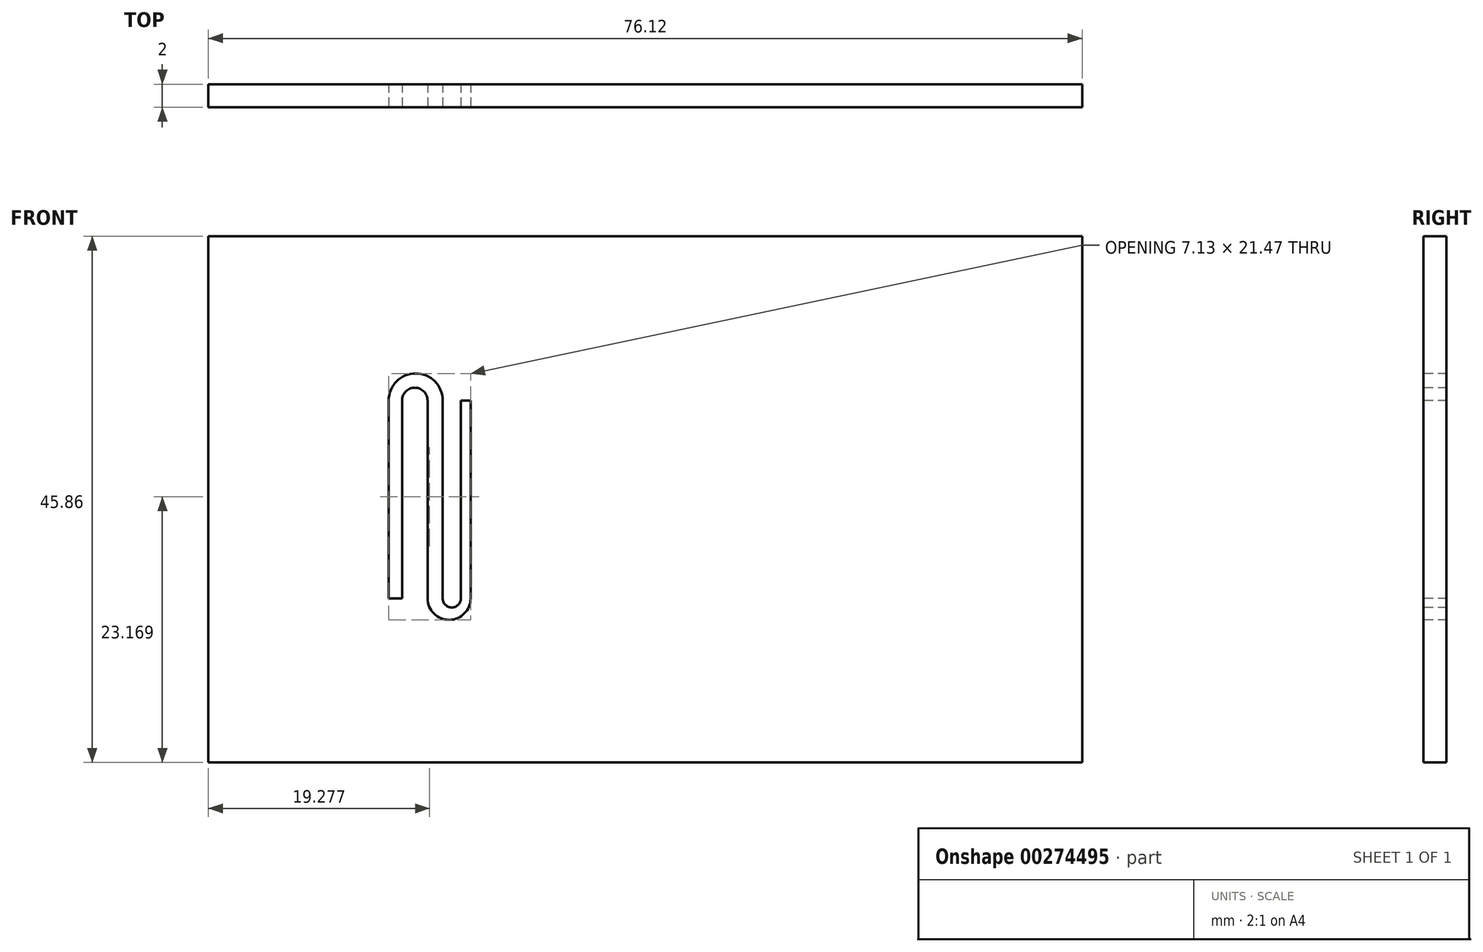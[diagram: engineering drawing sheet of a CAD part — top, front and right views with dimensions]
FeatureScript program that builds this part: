
annotation { "Feature Type Name" : "Feature", "Feature Type Description" : "" }
export const myFeature = defineFeature(function(context is Context, id is Id, definition is map)
    precondition{}
    {
        {
            var Q0;
            Q0=qCreatedBy(makeId("Front.planeOp"),FACE);
            var sketch = newSketch(context, id + "F0", { "sketchPlane" : qUnion([Q0])});
            skLineSegment(sketch, "E0.bottom", {"start": v(38.06, -22.93) * mm, "end": v(-38.06, -22.93) * mm});
            skLineSegment(sketch, "E0.top", {"start": v(38.06, 22.93) * mm, "end": v(-38.06, 22.93) * mm});
            skLineSegment(sketch, "E0.left", {"start": v(38.06, -22.93) * mm, "end": v(38.06, 22.93) * mm});
            skLineSegment(sketch, "E0.right", {"start": v(-38.06, -22.93) * mm, "end": v(-38.06, 22.93) * mm});
            skPoint(sketch, "E0.middle", {"position": v(0, 0) * mm});
            skSolve(sketch);
        }
        {
            var Q0;
            Q0=makeQuery(id+"F0.imprint","IMPRINT",FACE,{"disambiguationData":[TD([[makeQuery(id+"F0.imprint","IMPRINT",EDGE,{"derivedFrom":sQuery(id+"F0.wireOp",EDGE,"E0.bottom")}),-1.0]])]});
            extrude(context, id + "F1", {"entities" : qUnion([Q0]), "depth" : 2 * mm});
        }
        {
            var Q0;
            Q0=makeQuery(id+"F1.opExtrude","CAP_FACE",FACE,{"disambiguationData":[OSD([sQuery(id+"F0.wireOp",EDGE,"E0.bottom"),sQuery(id+"F0.wireOp",EDGE,"E0.top"),sQuery(id+"F0.wireOp",EDGE,"E0.left"),sQuery(id+"F0.wireOp",EDGE,"E0.right")])],"isStart":false});
            var sketch = newSketch(context, id + "F2", { "sketchPlane" : qUnion([Q0])});
            skLineSegment(sketch, "E1.left", {"start": v(21.19, -8.62) * mm, "end": v(21.19, 8.62) * mm});
            skLineSegment(sketch, "E1.right", {"start": v(-21.19, -8.62) * mm, "end": v(-21.19, 8.62) * mm});
            skPoint(sketch, "E1.middle", {"position": v(0, 0) * mm});
            skLineSegment(sketch, "E2", {"start": v(-18.96, 8.62) * mm, "end": v(-18.96, -8.62) * mm});
            skArc(sketch, "E3", {"start": v(-18.96, 8.62) * mm, "mid": v(-20.08, 9.73) * mm, "end": v(-21.19, 8.62) * mm});
            skLineSegment(sketch, "E4", {"start": v(-22.35, -8.62) * mm, "end": v(-22.35, 8.62) * mm});
            skLineSegment(sketch, "E5", {"start": v(-17.65, 8.62) * mm, "end": v(-17.65, -8.62) * mm});
            skArc(sketch, "E6", {"start": v(-17.65, 8.62) * mm, "mid": v(-20, 10.97) * mm, "end": v(-22.35, 8.62) * mm});
            skLineSegment(sketch, "E7", {"start": v(-22.35, -8.62) * mm, "end": v(-21.19, -8.62) * mm});
            skLineSegment(sketch, "E8", {"start": v(-16.06, -8.62) * mm, "end": v(-16.06, 8.62) * mm});
            skLineSegment(sketch, "E9", {"start": v(-16.06, 8.62) * mm, "end": v(-15.22, 8.62) * mm});
            skLineSegment(sketch, "E10", {"start": v(-15.22, 8.62) * mm, "end": v(-15.22, -8.62) * mm});
            skArc(sketch, "E11", {"start": v(-17.65, -8.62) * mm, "mid": v(-16.85, -9.42) * mm, "end": v(-16.06, -8.62) * mm});
            skArc(sketch, "E12", {"start": v(-18.96, -8.62) * mm, "mid": v(-17.1, -10.5) * mm, "end": v(-15.22, -8.62) * mm});
            skSolve(sketch);
        }
        {
            var Q0;
            Q0 = qSketchRegion(id + "F2", true);
            extrude(context, id + "F3", {"entities" : qUnion([Q0]), "operationType" : NewBodyOperationType.REMOVE, "endBound" : BoundingType.THROUGH_ALL, "oppositeDirection" : true, "depth" : 1 * mm});
        }
    });
